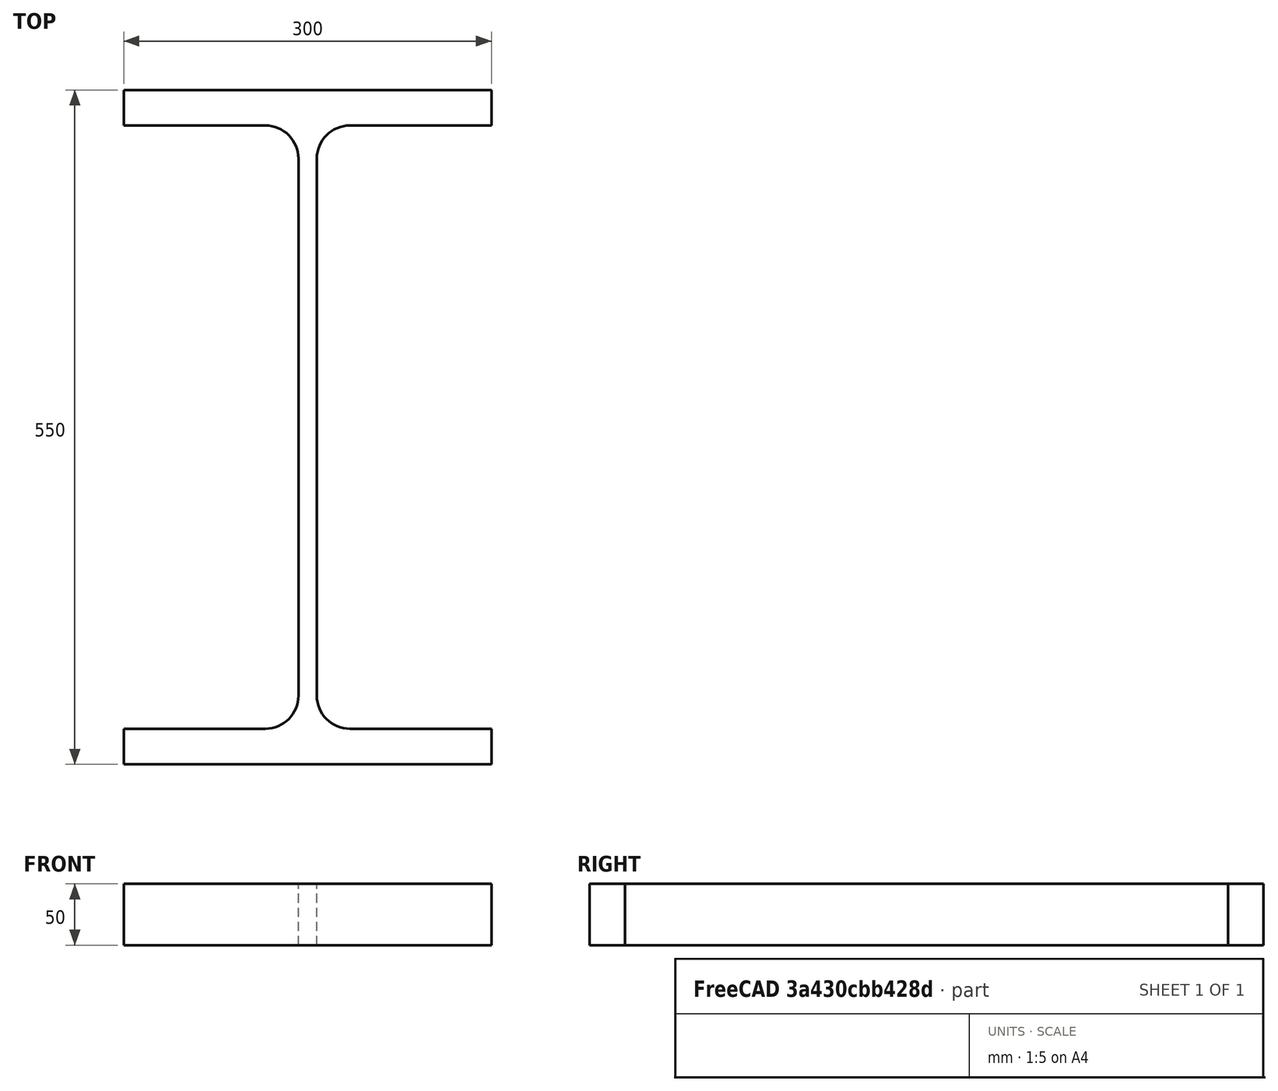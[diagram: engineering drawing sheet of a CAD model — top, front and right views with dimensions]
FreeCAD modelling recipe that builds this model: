
FCSTD DOCUMENT  (FreeCAD 0.15R4671 (Git))
Label: HE-B-Profile 550 DIN1025-2 S235JR
License: All rights reserved
LicenseURL: http://en.wikipedia.org/wiki/All_rights_reserved
objects: Sketcher::SketchObject×1, Part::Extrusion×1
note: 2 computed .brp shape members not serialized (recipe doc carries the construction recipe); baked Part::Feature solids carry a one-line shape summary decoded from their .brp

FEATURE [Sketcher::SketchObject] Sketch
  sketch-geometry (16):
    g0: LineSegment StartX=7.5 StartY=-219 StartZ=0 EndX=7.5 EndY=219 EndZ=0
    g1: LineSegment StartX=34.5 StartY=246 StartZ=0 EndX=150 EndY=246 EndZ=0
    g2: LineSegment StartX=150 StartY=246 StartZ=0 EndX=150 EndY=275 EndZ=0
    g3: LineSegment StartX=150 StartY=275 StartZ=0 EndX=-150 EndY=275 EndZ=0
    g4: LineSegment StartX=-150 StartY=275 StartZ=0 EndX=-150 EndY=246 EndZ=0
    g5: LineSegment StartX=-150 StartY=246 StartZ=0 EndX=-34.5 EndY=246 EndZ=0
    g6: LineSegment StartX=-7.5 StartY=219 StartZ=0 EndX=-7.5 EndY=-219 EndZ=0
    g7: LineSegment StartX=-34.5 StartY=-246 StartZ=0 EndX=-150 EndY=-246 EndZ=0
    g8: LineSegment StartX=-150 StartY=-246 StartZ=0 EndX=-150 EndY=-275 EndZ=0
    g9: LineSegment StartX=-150 StartY=-275 StartZ=0 EndX=150 EndY=-275 EndZ=0
    g10: LineSegment StartX=150 StartY=-275 StartZ=0 EndX=150 EndY=-246 EndZ=0
    g11: LineSegment StartX=150 StartY=-246 StartZ=0 EndX=34.5 EndY=-246 EndZ=0
    g12: ArcOfCircle CenterX=34.5 CenterY=219 CenterZ=0 NormalX=0 NormalY=0 NormalZ=1 Radius=27 StartAngle=1.5708 EndAngle=3.14159
    g13: ArcOfCircle CenterX=34.5 CenterY=-219 CenterZ=0 NormalX=0 NormalY=0 NormalZ=1 Radius=27 StartAngle=3.14159 EndAngle=4.71239
    g14: ArcOfCircle CenterX=-34.5 CenterY=219 CenterZ=0 NormalX=0 NormalY=0 NormalZ=1 Radius=27 StartAngle=0 EndAngle=1.5708
    g15: ArcOfCircle CenterX=-34.5 CenterY=-219 CenterZ=0 NormalX=0 NormalY=0 NormalZ=1 Radius=27 StartAngle=4.71239 EndAngle=6.28319
  constraints (42):
    c: Vertical(g0)
    c: Coincident(g2,g1)
    c: Vertical(g2)
    c: Coincident(g3,g2)
    c: Coincident(g4,g3)
    c: Vertical(g4)
    c: Coincident(g5,g4)
    c: Horizontal(g5)
    c: Vertical(g6)
    c: Horizontal(g7)
    c: Coincident(g8,g7)
    c: Vertical(g8)
    c: Coincident(g9,g8)
    c: Horizontal(g9)
    c: Coincident(g10,g9)
    c: Vertical(g10)
    c: Coincident(g11,g10)
    c: Horizontal(g11)
    c: Tangent(g1,g12) = 1.5708
    c: Tangent(g0,g12) = 1.5708
    c: Tangent(g0,g13) = 1.5708
    c: Tangent(g11,g13) = 1.5708
    c: Tangent(g5,g14) = 1.5708
    c: Tangent(g6,g14) = 1.5708
    c: Tangent(g6,g15) = 1.5708
    c: Tangent(g7,g15) = 1.5708
    c: Equal(g3,g9)
    c: Equal(g2,g4)
    c: Equal(g4,g8)
    c: Equal(g8,g10)
    c: Equal(g12,g14)
    c: Equal(g14,g15)
    c: Equal(g15,g13)
    c: Symmetric(g2,g3,g-2)
    c: Symmetric(g9,g8,g-2)
    c: Symmetric(g0,g6,g-2)
    c: Symmetric(g2,g9,g-1)
    c: DistanceY(g2,g9) = -550
    c: DistanceX(g3) = -300
    c: DistanceX(g0,g6) = -15
    c: DistanceY(g2) = 29
    c: Radius(g12) = 27
FEATURE [Part::Extrusion] Extrude  label="HE-B-Profile 550 DIN1025-2 S235JR"
  Base = -> Sketch
  Dir = (0,0,50)
  Solid = true
